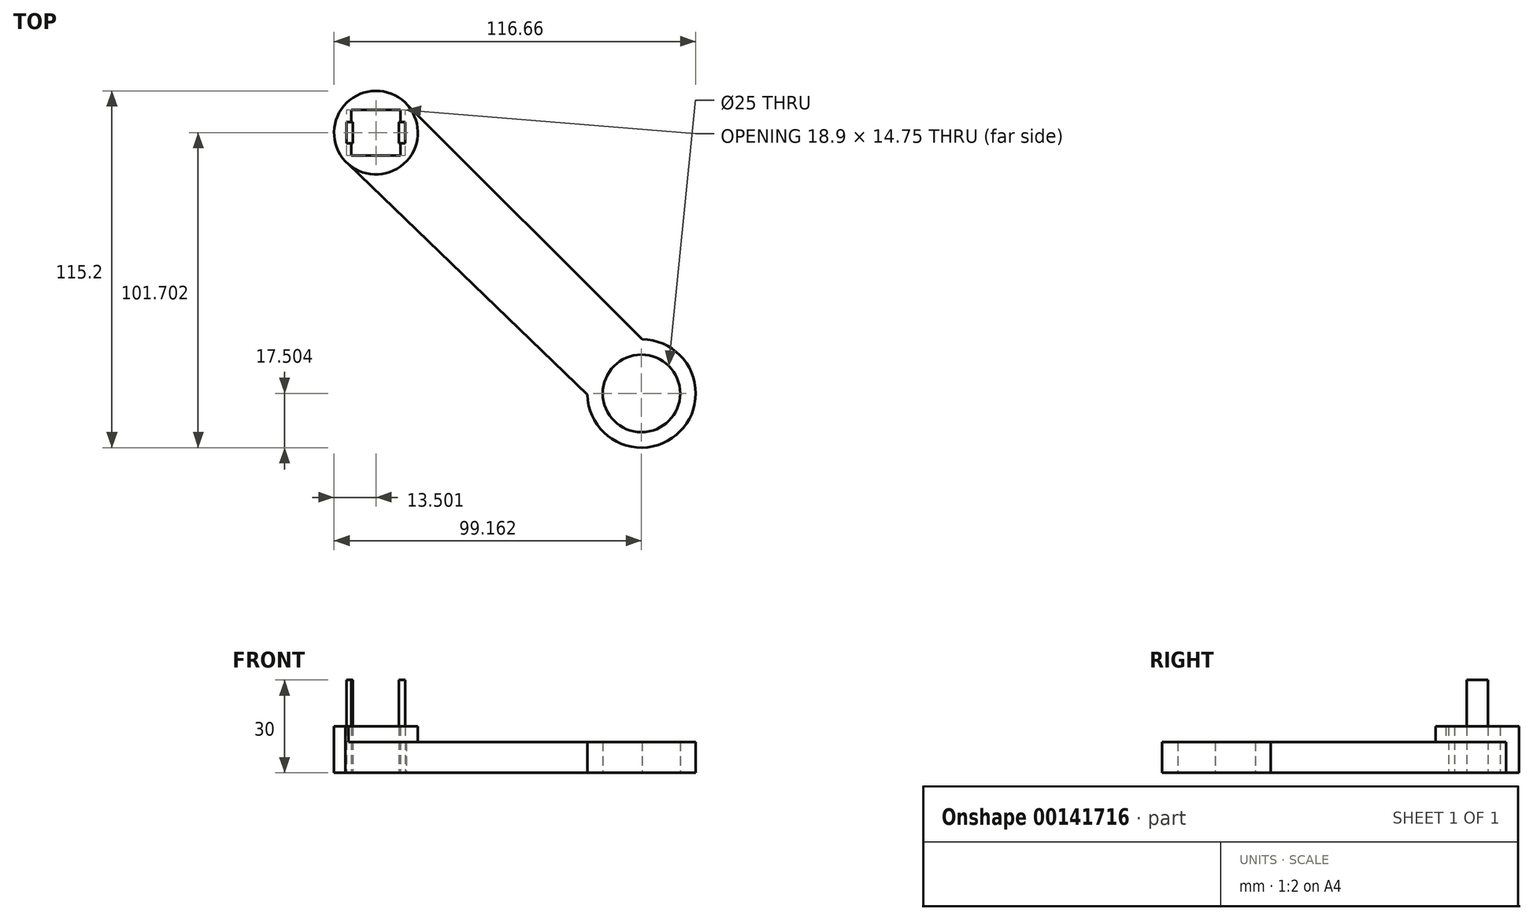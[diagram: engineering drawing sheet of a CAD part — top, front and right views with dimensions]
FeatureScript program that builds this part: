
annotation { "Feature Type Name" : "Feature", "Feature Type Description" : "" }
export const myFeature = defineFeature(function(context is Context, id is Id, definition is map)
    precondition{}
    {
        {
            var Q0;
            Q0=qCreatedBy(makeId("Top.planeOp"),FACE);
            var sketch = newSketch(context, id + "F0", { "sketchPlane" : qUnion([Q0])});
            skCircle(sketch, "E0", {"center": v(-47.8, 43.14) * mm, "radius": 13.5 * mm});
            skPoint(sketch, "E0.first.point", {"position": v(-57.35, 52.69) * mm});
            skPoint(sketch, "E0.second.point", {"position": v(-36.06, 36.5) * mm});
            skPoint(sketch, "E0.third.point", {"position": v(-49.6, 29.76) * mm});
            skLineSegment(sketch, "E1", {"start": v(29.54, -32.06) * mm, "end": v(29.37, -31.88) * mm});
            skLineSegment(sketch, "E2.bottom", {"start": v(-55.76, 50.52) * mm, "end": v(-39.86, 50.52) * mm});
            skLineSegment(sketch, "E2.top", {"start": v(-55.76, 35.77) * mm, "end": v(-39.86, 35.77) * mm});
            skLineSegment(sketch, "E2.left", {"start": v(-55.76, 50.52) * mm, "end": v(-55.76, 46.57) * mm});
            skLineSegment(sketch, "E2.right", {"start": v(-39.86, 50.52) * mm, "end": v(-39.86, 46.57) * mm});
            skArc(sketch, "E3", {"start": v(20.36, -41.5) * mm, "mid": v(50.33, -53.33) * mm, "end": v(38.01, -23.56) * mm});
            skCircle(sketch, "E4", {"center": v(37.85, -41.06) * mm, "radius": 12.5 * mm});
            skLineSegment(sketch, "E5.trimOffspring", {"start": v(42.1, -29.56) * mm, "end": v(41.77, -29.18) * mm});
            skLineSegment(sketch, "E6.trimOffspring", {"start": v(25.95, -44.88) * mm, "end": v(26.36, -45.3) * mm});
            skLineSegment(sketch, "E7.trimOffspring", {"start": v(-47.73, 43.07) * mm, "end": v(-47.8, 43.14) * mm});
            skLineSegment(sketch, "E8", {"start": v(-37.97, 52.39) * mm, "end": v(38.01, -23.56) * mm});
            skLineSegment(sketch, "E9", {"start": v(-57.65, 33.9) * mm, "end": v(20.36, -41.5) * mm});
            skLineSegment(sketch, "E10.trimOffspring", {"start": v(46.35, -31.89) * mm, "end": v(47.02, -32.56) * mm});
            skLineSegment(sketch, "E11.bottom", {"start": v(-55.76, 46.57) * mm, "end": v(-55.26, 46.57) * mm});
            skLineSegment(sketch, "E11.top", {"start": v(-55.76, 39.72) * mm, "end": v(-55.26, 39.72) * mm});
            skLineSegment(sketch, "E11.right", {"start": v(-55.26, 46.57) * mm, "end": v(-55.26, 39.72) * mm});
            skLineSegment(sketch, "E12.bottom", {"start": v(-39.86, 46.57) * mm, "end": v(-40.36, 46.57) * mm});
            skLineSegment(sketch, "E12.top", {"start": v(-39.86, 39.72) * mm, "end": v(-40.36, 39.72) * mm});
            skLineSegment(sketch, "E12.right", {"start": v(-40.36, 46.57) * mm, "end": v(-40.36, 39.72) * mm});
            skLineSegment(sketch, "E13.bottom", {"start": v(-39.86, 46.57) * mm, "end": v(-38.36, 46.57) * mm});
            skLineSegment(sketch, "E13.top", {"start": v(-39.86, 39.72) * mm, "end": v(-38.36, 39.72) * mm});
            skLineSegment(sketch, "E13.right", {"start": v(-38.36, 46.57) * mm, "end": v(-38.36, 39.72) * mm});
            skLineSegment(sketch, "E14.bottom", {"start": v(-55.76, 46.57) * mm, "end": v(-57.26, 46.57) * mm});
            skLineSegment(sketch, "E14.top", {"start": v(-55.76, 39.75) * mm, "end": v(-57.26, 39.75) * mm});
            skLineSegment(sketch, "E14.right", {"start": v(-57.26, 46.57) * mm, "end": v(-57.26, 39.75) * mm});
            skLineSegment(sketch, "E15.trimOffspring", {"start": v(-39.86, 39.72) * mm, "end": v(-39.86, 35.77) * mm});
            skLineSegment(sketch, "E16.trimOffspring", {"start": v(-55.76, 39.75) * mm, "end": v(-55.76, 35.77) * mm});
            skSolve(sketch);
        }
        {
            var Q0;
            Q0=makeQuery(id+"F0.imprint","IMPRINT",FACE,{"disambiguationData":[TD([[makeQuery(id+"F0.imprint","IMPRINT",EDGE,{"derivedFrom":sQuery(id+"F0.wireOp",EDGE,"E11.bottom")}),-1.0]])]});
            var Q1;
            Q1=makeQuery(id+"F0.imprint","IMPRINT",FACE,{"disambiguationData":[TD([[makeQuery(id+"F0.imprint","IMPRINT",EDGE,{"derivedFrom":sQuery(id+"F0.wireOp",EDGE,"E12.bottom")}),1.0]])]});
            extrude(context, id + "F1", {"entities" : qUnion([Q0, Q1]), "depth" : 30 * mm});
        }
        {
            var Q0;
            {var subQ4=sQuery(id+"F0.wireOp",EDGE,"E2.bottom");Q0=makeQuery(id+"F0.imprint","IMPRINT",FACE,{"disambiguationData":[TD([[makeQuery(id+"F0.imprint","IMPRINT",EDGE,{"derivedFrom":subQ4}),1.0]])]});}
            extrude(context, id + "F2", {"entities" : qUnion([Q0]), "depth" : 15 * mm});
        }
        {
            var Q0;
            {var subQ5=sQuery(id+"F0.wireOp",EDGE,"E3");Q0=makeQuery(id+"F0.imprint","IMPRINT",FACE,{"disambiguationData":[TD([[makeQuery(id+"F0.imprint","IMPRINT",EDGE,{"derivedFrom":subQ5}),1.0]])]});}
            extrude(context, id + "F3", {"entities" : qUnion([Q0]), "operationType" : NewBodyOperationType.ADD, "depth" : 10 * mm});
        }
    });
